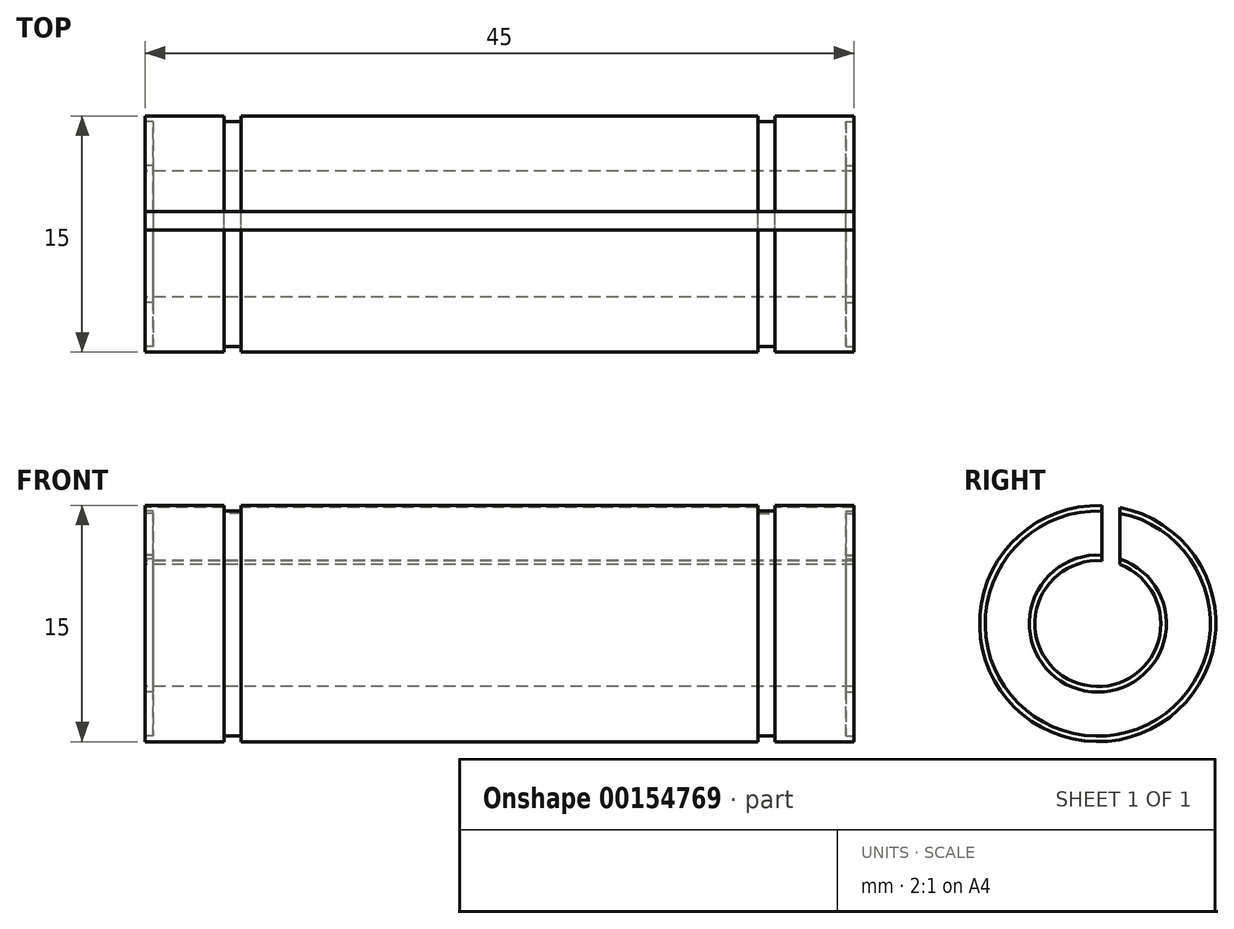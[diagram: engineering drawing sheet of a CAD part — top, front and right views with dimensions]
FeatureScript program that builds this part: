
annotation { "Feature Type Name" : "Feature", "Feature Type Description" : "" }
export const myFeature = defineFeature(function(context is Context, id is Id, definition is map)
    precondition{}
    {
        {
            var Q0;
            Q0=qCreatedBy(makeId("Right.planeOp"),FACE);
            var sketch = newSketch(context, id + "F0", { "sketchPlane" : qUnion([Q0])});
            skCircle(sketch, "E0", {"center": v(0, 0) * mm, "radius": 7.5 * mm});
            skCircle(sketch, "E1", {"center": v(0, 0) * mm, "radius": 4 * mm});
            skSolve(sketch);
        }
        {
            var Q0;
            Q0=makeQuery(id+"F0.imprint","IMPRINT",FACE,{"disambiguationData":[TD([[makeQuery(id+"F0.imprint","IMPRINT",EDGE,{"derivedFrom":sQuery(id+"F0.wireOp",EDGE,"E0")}),1.0]])]});
            extrude(context, id + "F1", {"entities" : qUnion([Q0]), "depth" : 45 * mm, "symmetric" : true});
        }
        {
            var Q0;
            Q0=qCreatedBy(makeId("Right.planeOp"),FACE);
            cPlane(context, id + "F2", {"entities" : qUnion([Q0]), "cplaneType" : CPlaneType.OFFSET, "offset" : 17.5 * mm, "width" : 150 * mm, "height" : 150 * mm});
        }
        {
            var Q0;
            Q0=qCreatedBy(makeId("Right.planeOp"),FACE);
            cPlane(context, id + "F3", {"entities" : qUnion([Q0]), "cplaneType" : CPlaneType.OFFSET, "offset" : 17.5 * mm, "oppositeDirection" : true, "width" : 150 * mm, "height" : 150 * mm});
        }
        {
            var Q0;
            Q0=qCreatedBy(id+"F3.planeOp",FACE);
            var sketch = newSketch(context, id + "F4", { "sketchPlane" : qUnion([Q0])});
            skCircle(sketch, "E2", {"center": v(0, 0) * mm, "radius": 7.15 * mm});
            skCircle(sketch, "E3", {"center": v(0, 0) * mm, "radius": 8 * mm});
            skSolve(sketch);
        }
        {
            var Q0;
            Q0 = qSketchRegion(id + "F4", true);
            extrude(context, id + "F5", {"entities" : qUnion([Q0]), "operationType" : NewBodyOperationType.REMOVE, "depth" : 1.1 * mm});
        }
        {
            var Q0;
            Q0=qCreatedBy(id+"F2.planeOp",FACE);
            var sketch = newSketch(context, id + "F6", { "sketchPlane" : qUnion([Q0])});
            skCircle(sketch, "E4", {"center": v(0, 0) * mm, "radius": 7.15 * mm});
            skCircle(sketch, "E5", {"center": v(0, 0) * mm, "radius": 8 * mm});
            skSolve(sketch);
        }
        {
            var Q0;
            Q0 = qSketchRegion(id + "F6", true);
            extrude(context, id + "F7", {"entities" : qUnion([Q0]), "operationType" : NewBodyOperationType.REMOVE, "oppositeDirection" : true, "depth" : 1.1 * mm});
        }
        {
            var Q0;
            Q0=makeQuery(id+"F1.opExtrude","CAP_FACE",FACE,{"disambiguationData":[OSD([sQuery(id+"F0.wireOp",EDGE,"E0"),sQuery(id+"F0.wireOp",EDGE,"E1")])],"isStart":false});
            var sketch = newSketch(context, id + "F8", { "sketchPlane" : qUnion([Q0])});
            skCircle(sketch, "E6", {"center": v(0, 0) * mm, "radius": 7.15 * mm});
            skCircle(sketch, "E7", {"center": v(0, 0) * mm, "radius": 4.35 * mm});
            skSolve(sketch);
        }
        {
            var Q0;
            Q0 = qSketchRegion(id + "F8", true);
            extrude(context, id + "F9", {"entities" : qUnion([Q0]), "operationType" : NewBodyOperationType.REMOVE, "oppositeDirection" : true, "depth" : 0.5 * mm});
        }
        {
            var Q0;
            Q0=makeQuery(id+"F1.opExtrude","CAP_FACE",FACE,{"disambiguationData":[OSD([sQuery(id+"F0.wireOp",EDGE,"E0"),sQuery(id+"F0.wireOp",EDGE,"E1")])],"isStart":true});
            var sketch = newSketch(context, id + "F10", { "sketchPlane" : qUnion([Q0])});
            skSolve(sketch);
        }
        {
            var Q0;
            Q0=makeQuery(id+"F10.imprint","IMPRINT",FACE,{"disambiguationData":[TD([[makeQuery(id+"F10.imprint","IMPRINT",EDGE,{"derivedFrom":makeQuery(id+"F1.opExtrude","CAP_EDGE",EDGE,{"disambiguationData":[OSD([sQuery(id+"F0.wireOp",EDGE,"E0")])],"isStart":true})}),-1.0]])]});
            var sketch = newSketch(context, id + "F11", { "sketchPlane" : qUnion([Q0])});
            skCircle(sketch, "E8", {"center": v(0, 0) * mm, "radius": 4.35 * mm});
            skCircle(sketch, "E9", {"center": v(0, 0) * mm, "radius": 7.15 * mm});
            skSolve(sketch);
        }
        {
            var Q0;
            Q0 = qSketchRegion(id + "F11", true);
            extrude(context, id + "F12", {"entities" : qUnion([Q0]), "operationType" : NewBodyOperationType.REMOVE, "oppositeDirection" : true, "depth" : 0.5 * mm});
        }
        {
            var Q0;
            Q0=makeQuery(id+"F9.boolean.opBoolean","COPY",FACE,{"derivedFrom":makeQuery(id+"F9.opExtrude","CAP_FACE",FACE,{"disambiguationData":[OSD([sQuery(id+"F8.wireOp",EDGE,"E6"),sQuery(id+"F8.wireOp",EDGE,"E7")])],"isStart":false})});
            var sketch = newSketch(context, id + "F13", { "sketchPlane" : qUnion([Q0])});
            skLineSegment(sketch, "E10.bottom", {"start": v(0.26, 15.15) * mm, "end": v(1.41, 15.15) * mm});
            skLineSegment(sketch, "E10.top", {"start": v(0.26, 0) * mm, "end": v(1.41, 0) * mm});
            skLineSegment(sketch, "E10.left", {"start": v(0.26, 15.15) * mm, "end": v(0.26, 0) * mm});
            skLineSegment(sketch, "E10.right", {"start": v(1.41, 15.15) * mm, "end": v(1.41, 0) * mm});
            skSolve(sketch);
        }
        {
            var Q0;
            Q0 = qSketchRegion(id + "F13", true);
            extrude(context, id + "F14", {"entities" : qUnion([Q0]), "operationType" : NewBodyOperationType.REMOVE, "oppositeDirection" : true, "depth" : 999 * mm, "offsetDistance" : 25 * mm, "symmetric" : true});
        }
    });
